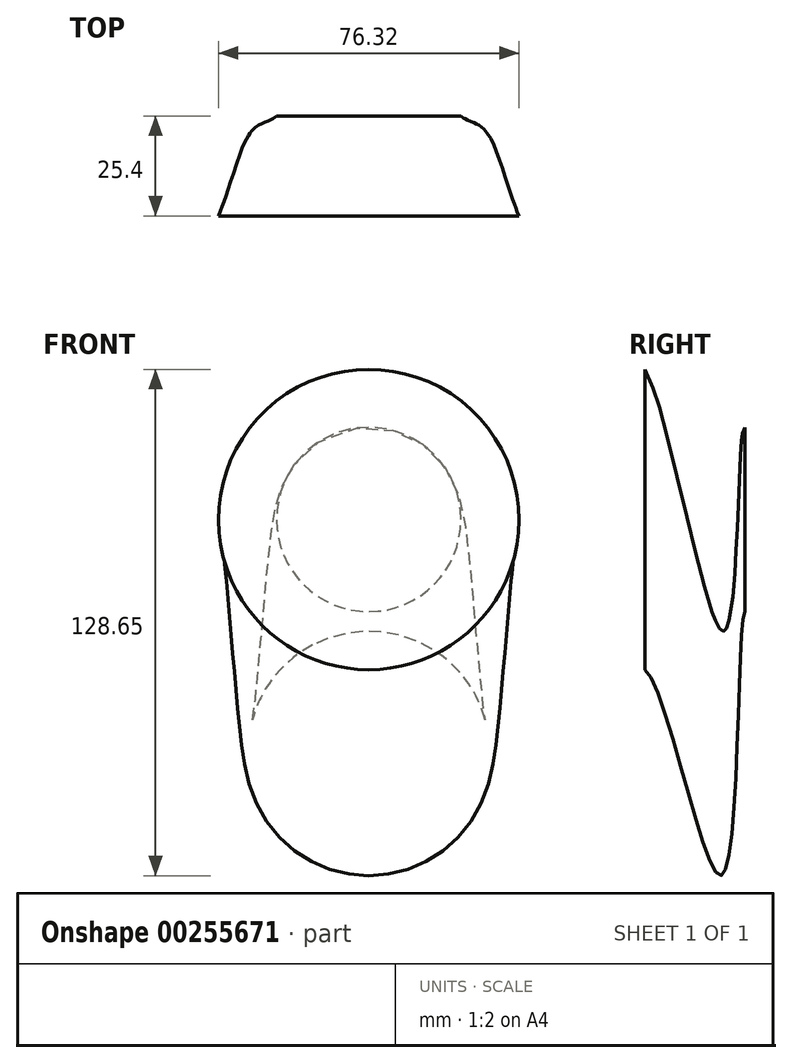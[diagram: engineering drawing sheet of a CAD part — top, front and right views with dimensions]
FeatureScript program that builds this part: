
annotation { "Feature Type Name" : "Feature", "Feature Type Description" : "" }
export const myFeature = defineFeature(function(context is Context, id is Id, definition is map)
    precondition{}
    {
        {
            var Q0;
            Q0=qCreatedBy(makeId("Front.planeOp"),FACE);
            cPlane(context, id + "F0", {"entities" : qUnion([Q0]), "cplaneType" : CPlaneType.OFFSET, "offset" : 25.4 * mm, "width" : 152.4 * mm, "height" : 152.4 * mm});
        }
        {
            var Q0;
            Q0=qCreatedBy(id+"F0.planeOp",FACE);
            var sketch = newSketch(context, id + "F1", { "sketchPlane" : qUnion([Q0])});
            skCircle(sketch, "E0", {"center": v(0, 0) * mm, "radius": 38.16 * mm});
            skSolve(sketch);
        }
        {
            var Q0;
            Q0=qCreatedBy(makeId("Front.planeOp"),FACE);
            var sketch = newSketch(context, id + "F2", { "sketchPlane" : qUnion([Q0])});
            skCircle(sketch, "E1", {"center": v(0, 0) * mm, "radius": 23.42 * mm});
            skSolve(sketch);
        }
        {
            var Q0;
            Q0=qCreatedBy(makeId("Right.planeOp"),FACE);
            var sketch = newSketch(context, id + "F3", { "sketchPlane" : qUnion([Q0])});
            skFitSpline(sketch, "E2", {"points": [v(-25.4, -38.16) * mm, v(-6.05, -90.48) * mm, v(0, -23.42) * mm], "startDerivative": vector(33.81, -21.3) * mm, "endDerivative": vector(12.6, 19.55) * mm});
            skSolve(sketch);
        }
        {
            var Q0;
            Q0=makeQuery(id+"F1.imprint","IMPRINT",FACE,{"disambiguationData":[TD([[makeQuery(id+"F1.imprint","IMPRINT",EDGE,{"derivedFrom":sQuery(id+"F1.wireOp",EDGE,"E0")}),1.0]])]});
            var Q1;
            Q1=makeQuery(id+"F2.imprint","IMPRINT",FACE,{"disambiguationData":[TD([[makeQuery(id+"F2.imprint","IMPRINT",EDGE,{"derivedFrom":sQuery(id+"F2.wireOp",EDGE,"E1")}),1.0]])]});
            var Q2;
            Q2=sQuery(id+"F3.wireOp",EDGE,"E2");
            loft(context, id + "F4", {"addGuides" : true, "sheetProfilesArray" : [{ "sheetProfileEntities" : qUnion([Q0]) }, { "sheetProfileEntities" : qUnion([Q1]) }], "guidesArray" : [{ "guideEntities" : qUnion([Q2]), "guideDerivativeType" : LoftGuideDerivativeType.DEFAULT, "guideDerivativeMagnitude" : 1 }]});
        }
    });
